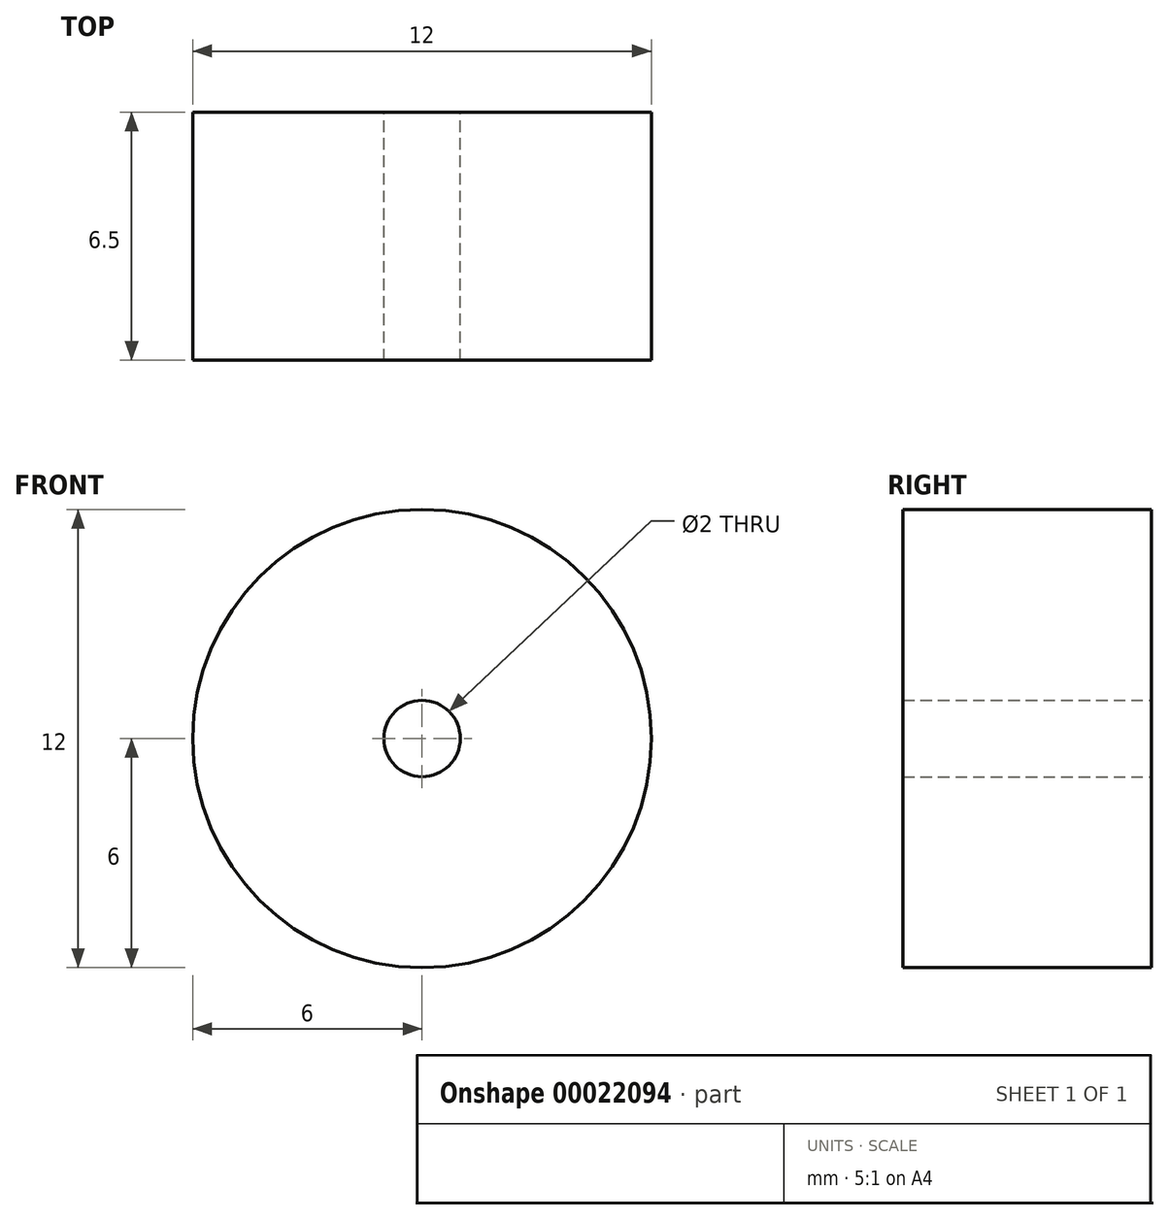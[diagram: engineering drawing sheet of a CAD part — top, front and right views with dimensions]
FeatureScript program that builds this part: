
annotation { "Feature Type Name" : "Feature", "Feature Type Description" : "" }
export const myFeature = defineFeature(function(context is Context, id is Id, definition is map)
    precondition{}
    {
        {
            var Q0;
            Q0=qCreatedBy(makeId("Front.planeOp"),FACE);
            var sketch = newSketch(context, id + "F0", { "sketchPlane" : qUnion([Q0])});
            skCircle(sketch, "E0", {"center": v(0, 0) * mm, "radius": 6 * mm});
            skCircle(sketch, "E1", {"center": v(0, 0) * mm, "radius": 1 * mm});
            skSolve(sketch);
        }
        {
            var Q0;
            Q0=makeQuery(id+"F0.imprint","IMPRINT",FACE,{"disambiguationData":[TD([[makeQuery(id+"F0.imprint","IMPRINT",EDGE,{"derivedFrom":sQuery(id+"F0.wireOp",EDGE,"E0")}),1.0]])]});
            extrude(context, id + "F1", {"entities" : qUnion([Q0]), "depth" : 6.5 * mm});
        }
    });
